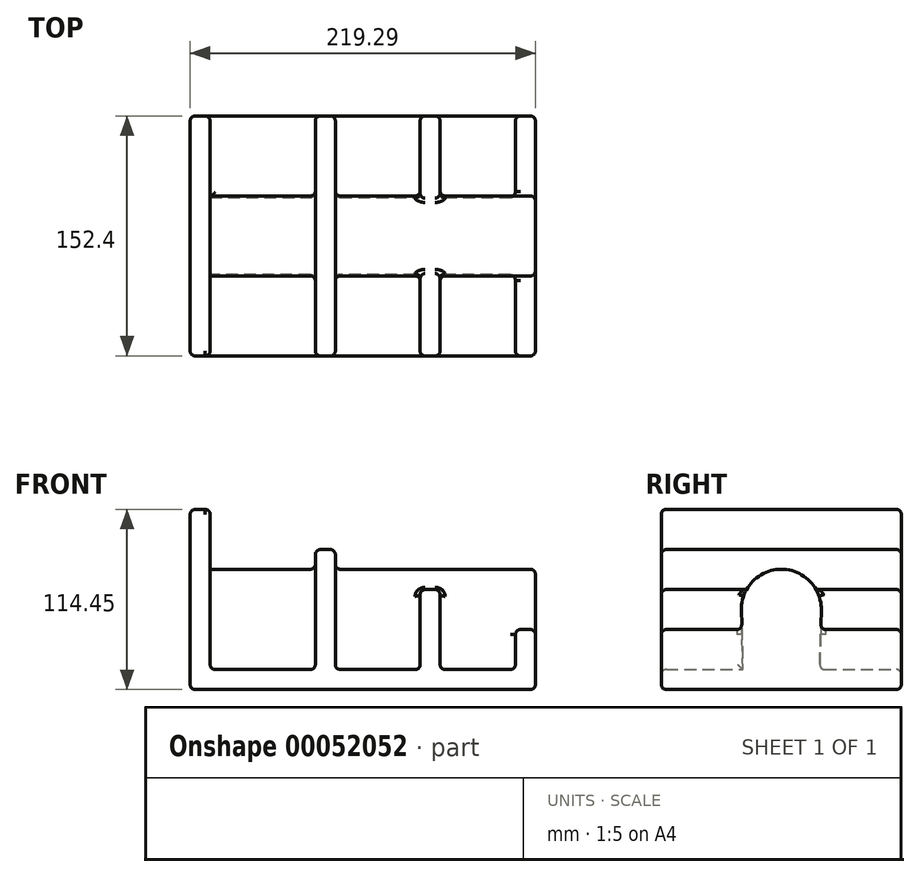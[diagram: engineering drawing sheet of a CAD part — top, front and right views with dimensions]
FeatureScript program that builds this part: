
annotation { "Feature Type Name" : "Feature", "Feature Type Description" : "" }
export const myFeature = defineFeature(function(context is Context, id is Id, definition is map)
    precondition{}
    {
        {
            var Q0;
            Q0=qCreatedBy(makeId("Front.planeOp"),FACE);
            var sketch = newSketch(context, id + "F0", { "sketchPlane" : qUnion([Q0])});
            skLineSegment(sketch, "E0", {"start": v(0, 114.3) * mm, "end": v(0, 0) * mm});
            skLineSegment(sketch, "E1", {"start": v(0, 0) * mm, "end": v(219.3, 0) * mm});
            skLineSegment(sketch, "E2", {"start": v(219.3, 0) * mm, "end": v(219.3, 38.1) * mm});
            skLineSegment(sketch, "E3", {"start": v(219.3, 38.1) * mm, "end": v(206.6, 38.1) * mm});
            skLineSegment(sketch, "E4", {"start": v(206.6, 38.1) * mm, "end": v(206.6, 12.7) * mm});
            skLineSegment(sketch, "E5", {"start": v(206.6, 12.7) * mm, "end": v(158.76, 12.7) * mm});
            skLineSegment(sketch, "E6", {"start": v(158.76, 12.7) * mm, "end": v(158.76, 63.5) * mm});
            skLineSegment(sketch, "E7", {"start": v(158.76, 63.5) * mm, "end": v(146.06, 63.5) * mm});
            skLineSegment(sketch, "E8", {"start": v(146.06, 63.5) * mm, "end": v(146.06, 12.7) * mm});
            skLineSegment(sketch, "E9", {"start": v(146.06, 12.7) * mm, "end": v(92.23, 12.7) * mm});
            skLineSegment(sketch, "E10", {"start": v(92.23, 12.7) * mm, "end": v(92.23, 88.9) * mm});
            skLineSegment(sketch, "E11", {"start": v(92.23, 88.9) * mm, "end": v(79.53, 88.9) * mm});
            skLineSegment(sketch, "E12", {"start": v(79.53, 88.9) * mm, "end": v(79.53, 12.7) * mm});
            skLineSegment(sketch, "E13", {"start": v(79.53, 12.7) * mm, "end": v(12.7, 12.7) * mm});
            skLineSegment(sketch, "E14", {"start": v(12.7, 12.7) * mm, "end": v(12.7, 114.5) * mm});
            skLineSegment(sketch, "E15", {"start": v(12.7, 114.5) * mm, "end": v(0, 114.3) * mm});
            skSolve(sketch);
        }
        {
            var Q0;
            Q0=makeQuery(id+"F0.imprint","IMPRINT",FACE,{"disambiguationData":[TD([[makeQuery(id+"F0.imprint","IMPRINT",EDGE,{"derivedFrom":sQuery(id+"F0.wireOp",EDGE,"E0")}),1.0]])]});
            extrude(context, id + "F1", {"entities" : qUnion([Q0]), "depth" : 152.4 * mm});
        }
        {
            var Q0;
            Q0=makeQuery(id+"F1.opExtrude","SWEPT_FACE",FACE,{"disambiguationData":[OSD([sQuery(id+"F0.wireOp",EDGE,"E14")])]});
            var sketch = newSketch(context, id + "F2", { "sketchPlane" : qUnion([Q0])});
            skArc(sketch, "E16", {"start": v(-50.8, 50.3) * mm, "mid": v(-76.17, 76.4) * mm, "end": v(-101.6, 50.36) * mm});
            skLineSegment(sketch, "E17", {"start": v(-101.6, 50.36) * mm, "end": v(-100.64, 12.7) * mm});
            skLineSegment(sketch, "E18", {"start": v(-100.64, 12.7) * mm, "end": v(-51.85, 12.7) * mm});
            skLineSegment(sketch, "E19", {"start": v(-51.85, 12.7) * mm, "end": v(-50.8, 50.3) * mm});
            skSolve(sketch);
        }
        {
            var Q0;
            Q0 = qSketchRegion(id + "F2", true);
            var Q1;
            Q1=makeQuery(id+"F1.opExtrude","SWEPT_FACE",FACE,{"disambiguationData":[OSD([sQuery(id+"F0.wireOp",EDGE,"E2")])]});
            extrude(context, id + "F3", {"entities" : qUnion([Q0]), "operationType" : NewBodyOperationType.ADD, "endBound" : BoundingType.UP_TO_SURFACE, "endBoundEntityFace" : qUnion([Q1]), "depth" : 25.4 * mm});
        }
        {
            var Q0;
            Q0=makeQuery(id+"F1.opExtrude","CAP_EDGE",EDGE,{"disambiguationData":[OSD([sQuery(id+"F0.wireOp",EDGE,"E11")])],"isStart":false});
            var Q1;
            Q1=makeQuery(id+"F1.opExtrude","CAP_EDGE",EDGE,{"disambiguationData":[OSD([sQuery(id+"F0.wireOp",EDGE,"E7")])],"isStart":false});
            var Q2;
            Q2=makeQuery(id+"F1.opExtrude","CAP_EDGE",EDGE,{"disambiguationData":[OSD([sQuery(id+"F0.wireOp",EDGE,"E3")])],"isStart":true});
            var Q3;
            Q3=makeQuery(id+"F1.opExtrude","CAP_EDGE",EDGE,{"disambiguationData":[OSD([sQuery(id+"F0.wireOp",EDGE,"E14")])],"isStart":false});
            var Q4;
            Q4=makeQuery(id+"F1.opExtrude","CAP_EDGE",EDGE,{"disambiguationData":[OSD([sQuery(id+"F0.wireOp",EDGE,"E10")])],"isStart":true});
            var Q5;
            Q5=makeQuery(id+"F1.opExtrude","CAP_EDGE",EDGE,{"disambiguationData":[OSD([sQuery(id+"F0.wireOp",EDGE,"E6")])],"isStart":false});
            var Q6;
            Q6=makeQuery(id+"F1.opExtrude","CAP_EDGE",EDGE,{"disambiguationData":[OSD([sQuery(id+"F0.wireOp",EDGE,"E9")])],"isStart":true});
            var Q7;
            Q7=makeQuery(id+"F1.opExtrude","CAP_EDGE",EDGE,{"disambiguationData":[OSD([sQuery(id+"F0.wireOp",EDGE,"E1")])],"isStart":true});
            var Q8;
            Q8=makeQuery(id+"F1.opExtrude","CAP_EDGE",EDGE,{"disambiguationData":[OSD([sQuery(id+"F0.wireOp",EDGE,"E8")])],"isStart":true});
            var Q9;
            Q9=makeQuery(id+"F1.opExtrude","SWEPT_EDGE",EDGE,{"disambiguationData":[OSD([sQuery(id+"F0.wireOp",EDGE,"E14"),sQuery(id+"F0.wireOp",EDGE,"E15")])]});
            var Q10;
            Q10=makeQuery(id+"F1.opExtrude","CAP_EDGE",EDGE,{"disambiguationData":[OSD([sQuery(id+"F0.wireOp",EDGE,"E6")])],"isStart":true});
            var Q11;
            Q11=makeQuery(id+"F1.opExtrude","SWEPT_EDGE",EDGE,{"disambiguationData":[OSD([sQuery(id+"F0.wireOp",EDGE,"E0"),sQuery(id+"F0.wireOp",EDGE,"E15")])]});
            var Q12;
            Q12=makeQuery(id+"F1.opExtrude","CAP_EDGE",EDGE,{"disambiguationData":[OSD([sQuery(id+"F0.wireOp",EDGE,"E5")])],"isStart":true});
            var Q13;
            Q13=makeQuery(id+"F1.opExtrude","SWEPT_EDGE",EDGE,{"disambiguationData":[OSD([sQuery(id+"F0.wireOp",EDGE,"E1"),sQuery(id+"F0.wireOp",EDGE,"E2")])]});
            var Q14;
            Q14=makeQuery(id+"F1.opExtrude","CAP_EDGE",EDGE,{"disambiguationData":[OSD([sQuery(id+"F0.wireOp",EDGE,"E13")])],"isStart":true});
            var Q15;
            Q15=makeQuery(id+"F3.opExtrude","CAP_EDGE",EDGE,{"disambiguationData":[OSD([sQuery(id+"F2.wireOp",EDGE,"E16")])],"isStart":false});
            var Q16;
            Q16=makeQuery(id+"F1.opExtrude","CAP_EDGE",EDGE,{"disambiguationData":[OSD([sQuery(id+"F0.wireOp",EDGE,"E12")])],"isStart":true});
            var Q17;
            {var subQ0=sQuery(id+"F0.wireOp",EDGE,"E7");var subQ1=sQuery(id+"F0.wireOp",EDGE,"E6");Q17=makeQuery(id+"F3.boolean.opBoolean","SPLIT",EDGE,{"disambiguationData":[TD([makeQuery(id+"F1.opExtrude","CAP_FACE",FACE,{"disambiguationData":[OSD([sQuery(id+"F0.wireOp",EDGE,"E0"),sQuery(id+"F0.wireOp",EDGE,"E1"),sQuery(id+"F0.wireOp",EDGE,"E2"),sQuery(id+"F0.wireOp",EDGE,"E3"),sQuery(id+"F0.wireOp",EDGE,"E4"),sQuery(id+"F0.wireOp",EDGE,"E5"),subQ1,subQ0,sQuery(id+"F0.wireOp",EDGE,"E8"),sQuery(id+"F0.wireOp",EDGE,"E9"),sQuery(id+"F0.wireOp",EDGE,"E10"),sQuery(id+"F0.wireOp",EDGE,"E11"),sQuery(id+"F0.wireOp",EDGE,"E12"),sQuery(id+"F0.wireOp",EDGE,"E13"),sQuery(id+"F0.wireOp",EDGE,"E14"),sQuery(id+"F0.wireOp",EDGE,"E15")])],"isStart":true})])],"derivedFrom":makeQuery(id+"F1.opExtrude","SWEPT_EDGE",EDGE,{"disambiguationData":[OSD([subQ1,subQ0])]})});}
            var Q18;
            Q18=makeQuery(id+"F1.opExtrude","CAP_EDGE",EDGE,{"disambiguationData":[OSD([sQuery(id+"F0.wireOp",EDGE,"E10")])],"isStart":false});
            var Q19;
            Q19=makeQuery(id+"F1.opExtrude","SWEPT_EDGE",EDGE,{"disambiguationData":[OSD([sQuery(id+"F0.wireOp",EDGE,"E10"),sQuery(id+"F0.wireOp",EDGE,"E11")])]});
            var Q20;
            Q20=makeQuery(id+"F1.opExtrude","SWEPT_EDGE",EDGE,{"disambiguationData":[OSD([sQuery(id+"F0.wireOp",EDGE,"E11"),sQuery(id+"F0.wireOp",EDGE,"E12")])]});
            var Q21;
            Q21=makeQuery(id+"F3.opExtrude","CAP_EDGE",EDGE,{"disambiguationData":[OSD([sQuery(id+"F2.wireOp",EDGE,"E16")])],"isStart":true});
            var Q22;
            {var subQ0=sQuery(id+"F0.wireOp",EDGE,"E8");var subQ1=sQuery(id+"F0.wireOp",EDGE,"E7");Q22=makeQuery(id+"F3.boolean.opBoolean","SPLIT",EDGE,{"disambiguationData":[TD([makeQuery(id+"F1.opExtrude","CAP_FACE",FACE,{"disambiguationData":[OSD([sQuery(id+"F0.wireOp",EDGE,"E0"),sQuery(id+"F0.wireOp",EDGE,"E1"),sQuery(id+"F0.wireOp",EDGE,"E2"),sQuery(id+"F0.wireOp",EDGE,"E3"),sQuery(id+"F0.wireOp",EDGE,"E4"),sQuery(id+"F0.wireOp",EDGE,"E5"),sQuery(id+"F0.wireOp",EDGE,"E6"),subQ1,subQ0,sQuery(id+"F0.wireOp",EDGE,"E9"),sQuery(id+"F0.wireOp",EDGE,"E10"),sQuery(id+"F0.wireOp",EDGE,"E11"),sQuery(id+"F0.wireOp",EDGE,"E12"),sQuery(id+"F0.wireOp",EDGE,"E13"),sQuery(id+"F0.wireOp",EDGE,"E14"),sQuery(id+"F0.wireOp",EDGE,"E15")])],"isStart":false})])],"derivedFrom":makeQuery(id+"F1.opExtrude","SWEPT_EDGE",EDGE,{"disambiguationData":[OSD([subQ1,subQ0])]})});}
            var Q23;
            {var subQ0=sQuery(id+"F2.wireOp",EDGE,"E16");var subQ1=sQuery(id+"F2.wireOp",EDGE,"E19");Q23=makeQuery(id+"F3.boolean.opBoolean","SPLIT",EDGE,{"disambiguationData":[TD([makeQuery(id+"F1.opExtrude","SWEPT_FACE",FACE,{"disambiguationData":[OSD([sQuery(id+"F0.wireOp",EDGE,"E8")])]})])],"derivedFrom":makeQuery(id+"F3.opExtrude","SWEPT_EDGE",EDGE,{"disambiguationData":[OSD([subQ0,subQ1])]})});}
            var Q24;
            {var subQ0=sQuery(id+"F2.wireOp",EDGE,"E19");var subQ1=sQuery(id+"F2.wireOp",EDGE,"E16");Q24=makeQuery(id+"F3.boolean.opBoolean","SPLIT",EDGE,{"disambiguationData":[TD([makeQuery(id+"F1.opExtrude","SWEPT_FACE",FACE,{"disambiguationData":[OSD([sQuery(id+"F0.wireOp",EDGE,"E2")])]})])],"derivedFrom":makeQuery(id+"F3.opExtrude","SWEPT_EDGE",EDGE,{"disambiguationData":[OSD([subQ1,subQ0])]})});}
            var Q25;
            {var subQ0=sQuery(id+"F0.wireOp",EDGE,"E3");var subQ1=sQuery(id+"F0.wireOp",EDGE,"E2");var subQ2=sQuery(id+"F2.wireOp",EDGE,"E19");Q25=makeQuery(id+"F3.boolean.opBoolean","SPLIT",EDGE,{"disambiguationData":[TD([makeQuery(id+"F3.opExtrude","SWEPT_FACE",FACE,{"disambiguationData":[OSD([subQ2])]})])],"derivedFrom":makeQuery(id+"F1.opExtrude","SWEPT_EDGE",EDGE,{"disambiguationData":[OSD([subQ1,subQ0])]})});}
            var Q26;
            {var subQ0=sQuery(id+"F2.wireOp",EDGE,"E17");var subQ1=sQuery(id+"F0.wireOp",EDGE,"E3");var subQ2=sQuery(id+"F0.wireOp",EDGE,"E2");Q26=makeQuery(id+"F3.boolean.opBoolean","SPLIT",EDGE,{"disambiguationData":[TD([makeQuery(id+"F3.opExtrude","SWEPT_FACE",FACE,{"disambiguationData":[OSD([subQ0])]})])],"derivedFrom":makeQuery(id+"F1.opExtrude","SWEPT_EDGE",EDGE,{"disambiguationData":[OSD([subQ2,subQ1])]})});}
            var Q27;
            {var subQ0=sQuery(id+"F0.wireOp",EDGE,"E4");var subQ1=sQuery(id+"F0.wireOp",EDGE,"E3");Q27=makeQuery(id+"F3.boolean.opBoolean","SPLIT",EDGE,{"disambiguationData":[TD([makeQuery(id+"F3.opExtrude","SWEPT_FACE",FACE,{"disambiguationData":[OSD([sQuery(id+"F2.wireOp",EDGE,"E19")])]})])],"derivedFrom":makeQuery(id+"F1.opExtrude","SWEPT_EDGE",EDGE,{"disambiguationData":[OSD([subQ1,subQ0])]})});}
            var Q28;
            {var subQ0=sQuery(id+"F0.wireOp",EDGE,"E4");var subQ1=sQuery(id+"F0.wireOp",EDGE,"E3");Q28=makeQuery(id+"F3.boolean.opBoolean","SPLIT",EDGE,{"disambiguationData":[TD([makeQuery(id+"F3.opExtrude","SWEPT_FACE",FACE,{"disambiguationData":[OSD([sQuery(id+"F2.wireOp",EDGE,"E17")])]})])],"derivedFrom":makeQuery(id+"F1.opExtrude","SWEPT_EDGE",EDGE,{"disambiguationData":[OSD([subQ1,subQ0])]})});}
            var Q29;
            Q29=makeQuery(id+"F3.boolean.opBoolean","INTERSECT",EDGE,{"disambiguationData":[OD(0.0)],"derivedFrom":[makeQuery(id+"F1.opExtrude","SWEPT_FACE",FACE,{"disambiguationData":[OSD([sQuery(id+"F0.wireOp",EDGE,"E7")])]}),makeQuery(id+"F3.opExtrude","SWEPT_FACE",FACE,{"disambiguationData":[OSD([sQuery(id+"F2.wireOp",EDGE,"E16")])]})]});
            var Q30;
            {var subQ0=sQuery(id+"F0.wireOp",EDGE,"E6");var subQ1=sQuery(id+"F0.wireOp",EDGE,"E5");Q30=makeQuery(id+"F3.boolean.opBoolean","SPLIT",EDGE,{"disambiguationData":[TD([makeQuery(id+"F3.opExtrude","SWEPT_FACE",FACE,{"disambiguationData":[OSD([sQuery(id+"F2.wireOp",EDGE,"E19")])]})])],"derivedFrom":makeQuery(id+"F1.opExtrude","SWEPT_EDGE",EDGE,{"disambiguationData":[OSD([subQ1,subQ0])]})});}
            var Q31;
            Q31=makeQuery(id+"F3.boolean.opBoolean","INTERSECT",EDGE,{"derivedFrom":[makeQuery(id+"F1.opExtrude","SWEPT_FACE",FACE,{"disambiguationData":[OSD([sQuery(id+"F0.wireOp",EDGE,"E6")])]}),makeQuery(id+"F3.opExtrude","SWEPT_FACE",FACE,{"disambiguationData":[OSD([sQuery(id+"F2.wireOp",EDGE,"E19")])]})]});
            var Q32;
            Q32=makeQuery(id+"F3.boolean.opBoolean","INTERSECT",EDGE,{"derivedFrom":[makeQuery(id+"F1.opExtrude","SWEPT_FACE",FACE,{"disambiguationData":[OSD([sQuery(id+"F0.wireOp",EDGE,"E3")])]}),makeQuery(id+"F3.opExtrude","SWEPT_FACE",FACE,{"disambiguationData":[OSD([sQuery(id+"F2.wireOp",EDGE,"E19")])]})]});
            var Q33;
            {var subQ0=sQuery(id+"F0.wireOp",EDGE,"E10");var subQ1=sQuery(id+"F0.wireOp",EDGE,"E9");Q33=makeQuery(id+"F3.boolean.opBoolean","SPLIT",EDGE,{"disambiguationData":[TD([makeQuery(id+"F3.opExtrude","SWEPT_FACE",FACE,{"disambiguationData":[OSD([sQuery(id+"F2.wireOp",EDGE,"E19")])]})])],"derivedFrom":makeQuery(id+"F1.opExtrude","SWEPT_EDGE",EDGE,{"disambiguationData":[OSD([subQ1,subQ0])]})});}
            var Q34;
            Q34=makeQuery(id+"F1.opExtrude","CAP_EDGE",EDGE,{"disambiguationData":[OSD([sQuery(id+"F0.wireOp",EDGE,"E5")])],"isStart":false});
            var Q35;
            Q35=makeQuery(id+"F1.opExtrude","CAP_EDGE",EDGE,{"disambiguationData":[OSD([sQuery(id+"F0.wireOp",EDGE,"E13")])],"isStart":false});
            var Q36;
            Q36=makeQuery(id+"F1.opExtrude","CAP_EDGE",EDGE,{"disambiguationData":[OSD([sQuery(id+"F0.wireOp",EDGE,"E4")])],"isStart":false});
            var Q37;
            Q37=makeQuery(id+"F1.opExtrude","CAP_EDGE",EDGE,{"disambiguationData":[OSD([sQuery(id+"F0.wireOp",EDGE,"E12")])],"isStart":false});
            var Q38;
            Q38=makeQuery(id+"F1.opExtrude","CAP_EDGE",EDGE,{"disambiguationData":[OSD([sQuery(id+"F0.wireOp",EDGE,"E3")])],"isStart":false});
            var Q39;
            Q39=makeQuery(id+"F3.boolean.opBoolean","INTERSECT",EDGE,{"disambiguationData":[OD(1.0)],"derivedFrom":[makeQuery(id+"F1.opExtrude","SWEPT_FACE",FACE,{"disambiguationData":[OSD([sQuery(id+"F0.wireOp",EDGE,"E7")])]}),makeQuery(id+"F3.opExtrude","SWEPT_FACE",FACE,{"disambiguationData":[OSD([sQuery(id+"F2.wireOp",EDGE,"E16")])]})]});
            var Q40;
            Q40=makeQuery(id+"F1.opExtrude","CAP_EDGE",EDGE,{"disambiguationData":[OSD([sQuery(id+"F0.wireOp",EDGE,"E15")])],"isStart":false});
            var Q41;
            Q41=makeQuery(id+"F1.opExtrude","CAP_EDGE",EDGE,{"disambiguationData":[OSD([sQuery(id+"F0.wireOp",EDGE,"E11")])],"isStart":true});
            var Q42;
            Q42=makeQuery(id+"F1.opExtrude","CAP_EDGE",EDGE,{"disambiguationData":[OSD([sQuery(id+"F0.wireOp",EDGE,"E2")])],"isStart":true});
            var Q43;
            Q43=makeQuery(id+"F1.opExtrude","CAP_EDGE",EDGE,{"disambiguationData":[OSD([sQuery(id+"F0.wireOp",EDGE,"E0")])],"isStart":true});
            var Q44;
            {var subQ0=sQuery(id+"F0.wireOp",EDGE,"E8");var subQ1=sQuery(id+"F0.wireOp",EDGE,"E7");Q44=makeQuery(id+"F3.boolean.opBoolean","SPLIT",EDGE,{"disambiguationData":[TD([makeQuery(id+"F1.opExtrude","CAP_FACE",FACE,{"disambiguationData":[OSD([sQuery(id+"F0.wireOp",EDGE,"E0"),sQuery(id+"F0.wireOp",EDGE,"E1"),sQuery(id+"F0.wireOp",EDGE,"E2"),sQuery(id+"F0.wireOp",EDGE,"E3"),sQuery(id+"F0.wireOp",EDGE,"E4"),sQuery(id+"F0.wireOp",EDGE,"E5"),sQuery(id+"F0.wireOp",EDGE,"E6"),subQ1,subQ0,sQuery(id+"F0.wireOp",EDGE,"E9"),sQuery(id+"F0.wireOp",EDGE,"E10"),sQuery(id+"F0.wireOp",EDGE,"E11"),sQuery(id+"F0.wireOp",EDGE,"E12"),sQuery(id+"F0.wireOp",EDGE,"E13"),sQuery(id+"F0.wireOp",EDGE,"E14"),sQuery(id+"F0.wireOp",EDGE,"E15")])],"isStart":true})])],"derivedFrom":makeQuery(id+"F1.opExtrude","SWEPT_EDGE",EDGE,{"disambiguationData":[OSD([subQ1,subQ0])]})});}
            var Q45;
            Q45=makeQuery(id+"F1.opExtrude","SWEPT_EDGE",EDGE,{"disambiguationData":[OSD([sQuery(id+"F0.wireOp",EDGE,"E0"),sQuery(id+"F0.wireOp",EDGE,"E1")])]});
            var Q46;
            Q46=makeQuery(id+"F1.opExtrude","CAP_EDGE",EDGE,{"disambiguationData":[OSD([sQuery(id+"F0.wireOp",EDGE,"E14")])],"isStart":true});
            var Q47;
            Q47=makeQuery(id+"F1.opExtrude","CAP_EDGE",EDGE,{"disambiguationData":[OSD([sQuery(id+"F0.wireOp",EDGE,"E4")])],"isStart":true});
            var Q48;
            {var subQ0=sQuery(id+"F0.wireOp",EDGE,"E7");var subQ1=sQuery(id+"F0.wireOp",EDGE,"E6");Q48=makeQuery(id+"F3.boolean.opBoolean","SPLIT",EDGE,{"disambiguationData":[TD([makeQuery(id+"F1.opExtrude","CAP_FACE",FACE,{"disambiguationData":[OSD([sQuery(id+"F0.wireOp",EDGE,"E0"),sQuery(id+"F0.wireOp",EDGE,"E1"),sQuery(id+"F0.wireOp",EDGE,"E2"),sQuery(id+"F0.wireOp",EDGE,"E3"),sQuery(id+"F0.wireOp",EDGE,"E4"),sQuery(id+"F0.wireOp",EDGE,"E5"),subQ1,subQ0,sQuery(id+"F0.wireOp",EDGE,"E8"),sQuery(id+"F0.wireOp",EDGE,"E9"),sQuery(id+"F0.wireOp",EDGE,"E10"),sQuery(id+"F0.wireOp",EDGE,"E11"),sQuery(id+"F0.wireOp",EDGE,"E12"),sQuery(id+"F0.wireOp",EDGE,"E13"),sQuery(id+"F0.wireOp",EDGE,"E14"),sQuery(id+"F0.wireOp",EDGE,"E15")])],"isStart":false})])],"derivedFrom":makeQuery(id+"F1.opExtrude","SWEPT_EDGE",EDGE,{"disambiguationData":[OSD([subQ1,subQ0])]})});}
            var Q49;
            Q49=makeQuery(id+"F1.opExtrude","CAP_EDGE",EDGE,{"disambiguationData":[OSD([sQuery(id+"F0.wireOp",EDGE,"E15")])],"isStart":true});
            var Q50;
            Q50=makeQuery(id+"F1.opExtrude","CAP_EDGE",EDGE,{"disambiguationData":[OSD([sQuery(id+"F0.wireOp",EDGE,"E7")])],"isStart":true});
            var Q51;
            Q51=makeQuery(id+"F1.opExtrude","CAP_EDGE",EDGE,{"disambiguationData":[OSD([sQuery(id+"F0.wireOp",EDGE,"E2")])],"isStart":false});
            var Q52;
            Q52=makeQuery(id+"F1.opExtrude","CAP_EDGE",EDGE,{"disambiguationData":[OSD([sQuery(id+"F0.wireOp",EDGE,"E9")])],"isStart":false});
            var Q53;
            Q53=makeQuery(id+"F1.opExtrude","CAP_EDGE",EDGE,{"disambiguationData":[OSD([sQuery(id+"F0.wireOp",EDGE,"E1")])],"isStart":false});
            var Q54;
            Q54=makeQuery(id+"F1.opExtrude","CAP_EDGE",EDGE,{"disambiguationData":[OSD([sQuery(id+"F0.wireOp",EDGE,"E8")])],"isStart":false});
            var Q55;
            Q55=makeQuery(id+"F1.opExtrude","CAP_EDGE",EDGE,{"disambiguationData":[OSD([sQuery(id+"F0.wireOp",EDGE,"E0")])],"isStart":false});
            var Q56;
            {var subQ0=sQuery(id+"F0.wireOp",EDGE,"E13");var subQ1=sQuery(id+"F0.wireOp",EDGE,"E14");var subQ2=sQuery(id+"F2.wireOp",EDGE,"E19");Q56=makeQuery(id+"F3.boolean.opBoolean","SPLIT",EDGE,{"disambiguationData":[TD([makeQuery(id+"F1.opExtrude","SWEPT_FACE",FACE,{"disambiguationData":[OSD([sQuery(id+"F0.wireOp",EDGE,"E12")])]})])],"derivedFrom":makeQuery(id+"F3.opExtrude","SWEPT_EDGE",EDGE,{"disambiguationData":[OSD([subQ0,subQ1,sQuery(id+"F2.wireOp",EDGE,"E18"),subQ2])]})});}
            var Q57;
            Q57=makeQuery(id+"F3.opExtrude","CAP_EDGE",EDGE,{"disambiguationData":[OSD([sQuery(id+"F2.wireOp",EDGE,"E17")])],"isStart":true});
            var Q58;
            Q58=makeQuery(id+"F3.opExtrude","CAP_EDGE",EDGE,{"disambiguationData":[OSD([sQuery(id+"F2.wireOp",EDGE,"E17")])],"isStart":false});
            var Q59;
            Q59=makeQuery(id+"F3.opExtrude","CAP_EDGE",EDGE,{"disambiguationData":[OSD([sQuery(id+"F2.wireOp",EDGE,"E19")])],"isStart":true});
            var Q60;
            Q60=makeQuery(id+"F3.opExtrude","CAP_EDGE",EDGE,{"disambiguationData":[OSD([sQuery(id+"F2.wireOp",EDGE,"E19")])],"isStart":false});
            var Q61;
            Q61=makeQuery(id+"F3.boolean.opBoolean","INTERSECT",EDGE,{"disambiguationData":[OD(0.0)],"derivedFrom":[makeQuery(id+"F1.opExtrude","SWEPT_FACE",FACE,{"disambiguationData":[OSD([sQuery(id+"F0.wireOp",EDGE,"E6")])]}),makeQuery(id+"F3.opExtrude","SWEPT_FACE",FACE,{"disambiguationData":[OSD([sQuery(id+"F2.wireOp",EDGE,"E16")])]})]});
            var Q62;
            Q62=makeQuery(id+"F3.boolean.opBoolean","INTERSECT",EDGE,{"derivedFrom":[makeQuery(id+"F1.opExtrude","SWEPT_FACE",FACE,{"disambiguationData":[OSD([sQuery(id+"F0.wireOp",EDGE,"E4")])]}),makeQuery(id+"F3.opExtrude","SWEPT_FACE",FACE,{"disambiguationData":[OSD([sQuery(id+"F2.wireOp",EDGE,"E19")])]})]});
            var Q63;
            {var subQ0=sQuery(id+"F0.wireOp",EDGE,"E14");var subQ1=sQuery(id+"F0.wireOp",EDGE,"E13");Q63=makeQuery(id+"F3.boolean.opBoolean","SPLIT",EDGE,{"disambiguationData":[TD([makeQuery(id+"F3.opExtrude","SWEPT_FACE",FACE,{"disambiguationData":[OSD([sQuery(id+"F2.wireOp",EDGE,"E19")])]})])],"derivedFrom":makeQuery(id+"F1.opExtrude","SWEPT_EDGE",EDGE,{"disambiguationData":[OSD([subQ1,subQ0])]})});}
            var Q64;
            {var subQ0=sQuery(id+"F2.wireOp",EDGE,"E17");Q64=makeQuery(id+"F3.boolean.opBoolean","SPLIT",EDGE,{"disambiguationData":[TD([makeQuery(id+"F1.opExtrude","SWEPT_FACE",FACE,{"disambiguationData":[OSD([sQuery(id+"F0.wireOp",EDGE,"E8")])]})])],"derivedFrom":makeQuery(id+"F3.opExtrude","SWEPT_EDGE",EDGE,{"disambiguationData":[OSD([sQuery(id+"F0.wireOp",EDGE,"E13"),sQuery(id+"F0.wireOp",EDGE,"E14"),subQ0,sQuery(id+"F2.wireOp",EDGE,"E18")])]})});}
            var Q65;
            {var subQ0=sQuery(id+"F0.wireOp",EDGE,"E13");var subQ1=sQuery(id+"F0.wireOp",EDGE,"E14");var subQ2=sQuery(id+"F2.wireOp",EDGE,"E17");Q65=makeQuery(id+"F3.boolean.opBoolean","SPLIT",EDGE,{"disambiguationData":[TD([makeQuery(id+"F1.opExtrude","SWEPT_FACE",FACE,{"disambiguationData":[OSD([sQuery(id+"F0.wireOp",EDGE,"E12")])]})])],"derivedFrom":makeQuery(id+"F3.opExtrude","SWEPT_EDGE",EDGE,{"disambiguationData":[OSD([subQ0,subQ1,subQ2,sQuery(id+"F2.wireOp",EDGE,"E18")])]})});}
            var Q66;
            Q66=makeQuery(id+"F3.boolean.opBoolean","INTERSECT",EDGE,{"derivedFrom":[makeQuery(id+"F1.opExtrude","SWEPT_FACE",FACE,{"disambiguationData":[OSD([sQuery(id+"F0.wireOp",EDGE,"E12")])]}),makeQuery(id+"F3.opExtrude","SWEPT_FACE",FACE,{"disambiguationData":[OSD([sQuery(id+"F2.wireOp",EDGE,"E19")])]})]});
            var Q67;
            {var subQ0=sQuery(id+"F0.wireOp",EDGE,"E5");var subQ1=sQuery(id+"F0.wireOp",EDGE,"E4");Q67=makeQuery(id+"F3.boolean.opBoolean","SPLIT",EDGE,{"disambiguationData":[TD([makeQuery(id+"F3.opExtrude","SWEPT_FACE",FACE,{"disambiguationData":[OSD([sQuery(id+"F2.wireOp",EDGE,"E19")])]})])],"derivedFrom":makeQuery(id+"F1.opExtrude","SWEPT_EDGE",EDGE,{"disambiguationData":[OSD([subQ1,subQ0])]})});}
            var Q68;
            {var subQ0=sQuery(id+"F0.wireOp",EDGE,"E5");var subQ1=sQuery(id+"F0.wireOp",EDGE,"E4");Q68=makeQuery(id+"F3.boolean.opBoolean","SPLIT",EDGE,{"disambiguationData":[TD([makeQuery(id+"F3.opExtrude","SWEPT_FACE",FACE,{"disambiguationData":[OSD([sQuery(id+"F2.wireOp",EDGE,"E17")])]})])],"derivedFrom":makeQuery(id+"F1.opExtrude","SWEPT_EDGE",EDGE,{"disambiguationData":[OSD([subQ1,subQ0])]})});}
            var Q69;
            Q69=makeQuery(id+"F3.boolean.opBoolean","INTERSECT",EDGE,{"derivedFrom":[makeQuery(id+"F1.opExtrude","SWEPT_FACE",FACE,{"disambiguationData":[OSD([sQuery(id+"F0.wireOp",EDGE,"E8")])]}),makeQuery(id+"F3.opExtrude","SWEPT_FACE",FACE,{"disambiguationData":[OSD([sQuery(id+"F2.wireOp",EDGE,"E17")])]})]});
            var Q70;
            Q70=makeQuery(id+"F3.boolean.opBoolean","INTERSECT",EDGE,{"disambiguationData":[OD(1.0)],"derivedFrom":[makeQuery(id+"F1.opExtrude","SWEPT_FACE",FACE,{"disambiguationData":[OSD([sQuery(id+"F0.wireOp",EDGE,"E6")])]}),makeQuery(id+"F3.opExtrude","SWEPT_FACE",FACE,{"disambiguationData":[OSD([sQuery(id+"F2.wireOp",EDGE,"E16")])]})]});
            var Q71;
            Q71=makeQuery(id+"F3.boolean.opBoolean","INTERSECT",EDGE,{"derivedFrom":[makeQuery(id+"F1.opExtrude","SWEPT_FACE",FACE,{"disambiguationData":[OSD([sQuery(id+"F0.wireOp",EDGE,"E12")])]}),makeQuery(id+"F3.opExtrude","SWEPT_FACE",FACE,{"disambiguationData":[OSD([sQuery(id+"F2.wireOp",EDGE,"E16")])]})]});
            var Q72;
            {var subQ0=sQuery(id+"F2.wireOp",EDGE,"E16");var subQ1=sQuery(id+"F2.wireOp",EDGE,"E17");Q72=makeQuery(id+"F3.boolean.opBoolean","SPLIT",EDGE,{"disambiguationData":[TD([makeQuery(id+"F1.opExtrude","SWEPT_FACE",FACE,{"disambiguationData":[OSD([sQuery(id+"F0.wireOp",EDGE,"E12")])]})])],"derivedFrom":makeQuery(id+"F3.opExtrude","SWEPT_EDGE",EDGE,{"disambiguationData":[OSD([subQ0,subQ1])]})});}
            var Q73;
            {var subQ0=sQuery(id+"F0.wireOp",EDGE,"E10");var subQ1=sQuery(id+"F0.wireOp",EDGE,"E9");Q73=makeQuery(id+"F3.boolean.opBoolean","SPLIT",EDGE,{"disambiguationData":[TD([makeQuery(id+"F3.opExtrude","SWEPT_FACE",FACE,{"disambiguationData":[OSD([sQuery(id+"F2.wireOp",EDGE,"E17")])]})])],"derivedFrom":makeQuery(id+"F1.opExtrude","SWEPT_EDGE",EDGE,{"disambiguationData":[OSD([subQ1,subQ0])]})});}
            var Q74;
            {var subQ0=sQuery(id+"F0.wireOp",EDGE,"E6");var subQ1=sQuery(id+"F0.wireOp",EDGE,"E5");Q74=makeQuery(id+"F3.boolean.opBoolean","SPLIT",EDGE,{"disambiguationData":[TD([makeQuery(id+"F3.opExtrude","SWEPT_FACE",FACE,{"disambiguationData":[OSD([sQuery(id+"F2.wireOp",EDGE,"E17")])]})])],"derivedFrom":makeQuery(id+"F1.opExtrude","SWEPT_EDGE",EDGE,{"disambiguationData":[OSD([subQ1,subQ0])]})});}
            var Q75;
            Q75=makeQuery(id+"F3.boolean.opBoolean","INTERSECT",EDGE,{"derivedFrom":[makeQuery(id+"F1.opExtrude","SWEPT_FACE",FACE,{"disambiguationData":[OSD([sQuery(id+"F0.wireOp",EDGE,"E8")])]}),makeQuery(id+"F3.opExtrude","SWEPT_FACE",FACE,{"disambiguationData":[OSD([sQuery(id+"F2.wireOp",EDGE,"E19")])]})]});
            var Q76;
            Q76=makeQuery(id+"F3.boolean.opBoolean","INTERSECT",EDGE,{"derivedFrom":[makeQuery(id+"F1.opExtrude","SWEPT_FACE",FACE,{"disambiguationData":[OSD([sQuery(id+"F0.wireOp",EDGE,"E10")])]}),makeQuery(id+"F3.opExtrude","SWEPT_FACE",FACE,{"disambiguationData":[OSD([sQuery(id+"F2.wireOp",EDGE,"E17")])]})]});
            var Q77;
            {var subQ0=sQuery(id+"F2.wireOp",EDGE,"E19");Q77=makeQuery(id+"F3.boolean.opBoolean","SPLIT",EDGE,{"disambiguationData":[TD([makeQuery(id+"F1.opExtrude","SWEPT_FACE",FACE,{"disambiguationData":[OSD([sQuery(id+"F0.wireOp",EDGE,"E4")])]})])],"derivedFrom":makeQuery(id+"F3.opExtrude","SWEPT_EDGE",EDGE,{"disambiguationData":[OSD([sQuery(id+"F0.wireOp",EDGE,"E13"),sQuery(id+"F0.wireOp",EDGE,"E14"),sQuery(id+"F2.wireOp",EDGE,"E18"),subQ0])]})});}
            var Q78;
            Q78=makeQuery(id+"F3.boolean.opBoolean","INTERSECT",EDGE,{"derivedFrom":[makeQuery(id+"F1.opExtrude","SWEPT_FACE",FACE,{"disambiguationData":[OSD([sQuery(id+"F0.wireOp",EDGE,"E3")])]}),makeQuery(id+"F3.opExtrude","SWEPT_FACE",FACE,{"disambiguationData":[OSD([sQuery(id+"F2.wireOp",EDGE,"E17")])]})]});
            var Q79;
            {var subQ0=sQuery(id+"F2.wireOp",EDGE,"E17");var subQ1=sQuery(id+"F2.wireOp",EDGE,"E16");Q79=makeQuery(id+"F3.boolean.opBoolean","SPLIT",EDGE,{"disambiguationData":[TD([makeQuery(id+"F1.opExtrude","SWEPT_FACE",FACE,{"disambiguationData":[OSD([sQuery(id+"F0.wireOp",EDGE,"E2")])]})])],"derivedFrom":makeQuery(id+"F3.opExtrude","SWEPT_EDGE",EDGE,{"disambiguationData":[OSD([subQ1,subQ0])]})});}
            var Q80;
            {var subQ0=sQuery(id+"F2.wireOp",EDGE,"E16");var subQ1=sQuery(id+"F2.wireOp",EDGE,"E19");Q80=makeQuery(id+"F3.boolean.opBoolean","SPLIT",EDGE,{"disambiguationData":[TD([makeQuery(id+"F1.opExtrude","SWEPT_FACE",FACE,{"disambiguationData":[OSD([sQuery(id+"F0.wireOp",EDGE,"E12")])]})])],"derivedFrom":makeQuery(id+"F3.opExtrude","SWEPT_EDGE",EDGE,{"disambiguationData":[OSD([subQ0,subQ1])]})});}
            var Q81;
            Q81=makeQuery(id+"F3.boolean.opBoolean","INTERSECT",EDGE,{"derivedFrom":[makeQuery(id+"F1.opExtrude","SWEPT_FACE",FACE,{"disambiguationData":[OSD([sQuery(id+"F0.wireOp",EDGE,"E4")])]}),makeQuery(id+"F3.opExtrude","SWEPT_FACE",FACE,{"disambiguationData":[OSD([sQuery(id+"F2.wireOp",EDGE,"E17")])]})]});
            var Q82;
            {var subQ0=sQuery(id+"F2.wireOp",EDGE,"E19");Q82=makeQuery(id+"F3.boolean.opBoolean","SPLIT",EDGE,{"disambiguationData":[TD([makeQuery(id+"F1.opExtrude","SWEPT_FACE",FACE,{"disambiguationData":[OSD([sQuery(id+"F0.wireOp",EDGE,"E8")])]})])],"derivedFrom":makeQuery(id+"F3.opExtrude","SWEPT_EDGE",EDGE,{"disambiguationData":[OSD([sQuery(id+"F0.wireOp",EDGE,"E13"),sQuery(id+"F0.wireOp",EDGE,"E14"),sQuery(id+"F2.wireOp",EDGE,"E18"),subQ0])]})});}
            var Q83;
            Q83=makeQuery(id+"F3.boolean.opBoolean","INTERSECT",EDGE,{"derivedFrom":[makeQuery(id+"F1.opExtrude","SWEPT_FACE",FACE,{"disambiguationData":[OSD([sQuery(id+"F0.wireOp",EDGE,"E6")])]}),makeQuery(id+"F3.opExtrude","SWEPT_FACE",FACE,{"disambiguationData":[OSD([sQuery(id+"F2.wireOp",EDGE,"E17")])]})]});
            var Q84;
            {var subQ0=sQuery(id+"F2.wireOp",EDGE,"E17");Q84=makeQuery(id+"F3.boolean.opBoolean","SPLIT",EDGE,{"disambiguationData":[TD([makeQuery(id+"F1.opExtrude","SWEPT_FACE",FACE,{"disambiguationData":[OSD([sQuery(id+"F0.wireOp",EDGE,"E4")])]})])],"derivedFrom":makeQuery(id+"F3.opExtrude","SWEPT_EDGE",EDGE,{"disambiguationData":[OSD([sQuery(id+"F0.wireOp",EDGE,"E13"),sQuery(id+"F0.wireOp",EDGE,"E14"),subQ0,sQuery(id+"F2.wireOp",EDGE,"E18")])]})});}
            var Q85;
            Q85=makeQuery(id+"F3.boolean.opBoolean","INTERSECT",EDGE,{"derivedFrom":[makeQuery(id+"F1.opExtrude","SWEPT_FACE",FACE,{"disambiguationData":[OSD([sQuery(id+"F0.wireOp",EDGE,"E12")])]}),makeQuery(id+"F3.opExtrude","SWEPT_FACE",FACE,{"disambiguationData":[OSD([sQuery(id+"F2.wireOp",EDGE,"E17")])]})]});
            var Q86;
            {var subQ0=sQuery(id+"F2.wireOp",EDGE,"E16");var subQ1=sQuery(id+"F2.wireOp",EDGE,"E17");Q86=makeQuery(id+"F3.boolean.opBoolean","SPLIT",EDGE,{"disambiguationData":[TD([makeQuery(id+"F1.opExtrude","SWEPT_FACE",FACE,{"disambiguationData":[OSD([sQuery(id+"F0.wireOp",EDGE,"E8")])]})])],"derivedFrom":makeQuery(id+"F3.opExtrude","SWEPT_EDGE",EDGE,{"disambiguationData":[OSD([subQ0,subQ1])]})});}
            var Q87;
            {var subQ0=sQuery(id+"F0.wireOp",EDGE,"E13");var subQ1=sQuery(id+"F0.wireOp",EDGE,"E12");Q87=makeQuery(id+"F3.boolean.opBoolean","SPLIT",EDGE,{"disambiguationData":[TD([makeQuery(id+"F3.opExtrude","SWEPT_FACE",FACE,{"disambiguationData":[OSD([sQuery(id+"F2.wireOp",EDGE,"E19")])]})])],"derivedFrom":makeQuery(id+"F1.opExtrude","SWEPT_EDGE",EDGE,{"disambiguationData":[OSD([subQ1,subQ0])]})});}
            var Q88;
            Q88=makeQuery(id+"F3.boolean.opBoolean","INTERSECT",EDGE,{"disambiguationData":[OD(1.0)],"derivedFrom":[makeQuery(id+"F1.opExtrude","SWEPT_FACE",FACE,{"disambiguationData":[OSD([sQuery(id+"F0.wireOp",EDGE,"E8")])]}),makeQuery(id+"F3.opExtrude","SWEPT_FACE",FACE,{"disambiguationData":[OSD([sQuery(id+"F2.wireOp",EDGE,"E16")])]})]});
            var Q89;
            Q89=makeQuery(id+"F3.boolean.opBoolean","INTERSECT",EDGE,{"derivedFrom":[makeQuery(id+"F1.opExtrude","SWEPT_FACE",FACE,{"disambiguationData":[OSD([sQuery(id+"F0.wireOp",EDGE,"E10")])]}),makeQuery(id+"F3.opExtrude","SWEPT_FACE",FACE,{"disambiguationData":[OSD([sQuery(id+"F2.wireOp",EDGE,"E19")])]})]});
            var Q90;
            Q90=makeQuery(id+"F3.boolean.opBoolean","INTERSECT",EDGE,{"disambiguationData":[OD(0.0)],"derivedFrom":[makeQuery(id+"F1.opExtrude","SWEPT_FACE",FACE,{"disambiguationData":[OSD([sQuery(id+"F0.wireOp",EDGE,"E8")])]}),makeQuery(id+"F3.opExtrude","SWEPT_FACE",FACE,{"disambiguationData":[OSD([sQuery(id+"F2.wireOp",EDGE,"E16")])]})]});
            var Q91;
            Q91=makeQuery(id+"F3.boolean.opBoolean","INTERSECT",EDGE,{"derivedFrom":[makeQuery(id+"F1.opExtrude","SWEPT_FACE",FACE,{"disambiguationData":[OSD([sQuery(id+"F0.wireOp",EDGE,"E10")])]}),makeQuery(id+"F3.opExtrude","SWEPT_FACE",FACE,{"disambiguationData":[OSD([sQuery(id+"F2.wireOp",EDGE,"E16")])]})]});
            var Q92;
            {var subQ0=sQuery(id+"F0.wireOp",EDGE,"E9");var subQ1=sQuery(id+"F0.wireOp",EDGE,"E8");Q92=makeQuery(id+"F3.boolean.opBoolean","SPLIT",EDGE,{"disambiguationData":[TD([makeQuery(id+"F3.opExtrude","SWEPT_FACE",FACE,{"disambiguationData":[OSD([sQuery(id+"F2.wireOp",EDGE,"E19")])]})])],"derivedFrom":makeQuery(id+"F1.opExtrude","SWEPT_EDGE",EDGE,{"disambiguationData":[OSD([subQ1,subQ0])]})});}
            var Q93;
            {var subQ0=sQuery(id+"F0.wireOp",EDGE,"E13");var subQ1=sQuery(id+"F0.wireOp",EDGE,"E12");Q93=makeQuery(id+"F3.boolean.opBoolean","SPLIT",EDGE,{"disambiguationData":[TD([makeQuery(id+"F3.opExtrude","SWEPT_FACE",FACE,{"disambiguationData":[OSD([sQuery(id+"F2.wireOp",EDGE,"E17")])]})])],"derivedFrom":makeQuery(id+"F1.opExtrude","SWEPT_EDGE",EDGE,{"disambiguationData":[OSD([subQ1,subQ0])]})});}
            var Q94;
            {var subQ0=sQuery(id+"F0.wireOp",EDGE,"E9");var subQ1=sQuery(id+"F0.wireOp",EDGE,"E8");Q94=makeQuery(id+"F3.boolean.opBoolean","SPLIT",EDGE,{"disambiguationData":[TD([makeQuery(id+"F3.opExtrude","SWEPT_FACE",FACE,{"disambiguationData":[OSD([sQuery(id+"F2.wireOp",EDGE,"E17")])]})])],"derivedFrom":makeQuery(id+"F1.opExtrude","SWEPT_EDGE",EDGE,{"disambiguationData":[OSD([subQ1,subQ0])]})});}
            var Q95;
            {var subQ0=sQuery(id+"F0.wireOp",EDGE,"E14");var subQ1=sQuery(id+"F0.wireOp",EDGE,"E13");Q95=makeQuery(id+"F3.boolean.opBoolean","SPLIT",EDGE,{"disambiguationData":[TD([makeQuery(id+"F3.opExtrude","SWEPT_FACE",FACE,{"disambiguationData":[OSD([sQuery(id+"F2.wireOp",EDGE,"E17")])]})])],"derivedFrom":makeQuery(id+"F1.opExtrude","SWEPT_EDGE",EDGE,{"disambiguationData":[OSD([subQ1,subQ0])]})});}
            fillet(context, id + "F4", {"entities" : qUnion([Q0, Q1, Q2, Q3, Q4, Q5, Q6, Q7, Q8, Q9, Q10, Q11, Q12, Q13, Q14, Q15, Q16, Q17, Q18, Q19, Q20, Q21, Q22, Q23, Q24, Q25, Q26, Q27, Q28, Q29, Q30, Q31, Q32, Q33, Q34, Q35, Q36, Q37, Q38, Q39, Q40, Q41, Q42, Q43, Q44, Q45, Q46, Q47, Q48, Q49, Q50, Q51, Q52, Q53, Q54, Q55, Q56, Q57, Q58, Q59, Q60, Q61, Q62, Q63, Q64, Q65, Q66, Q67, Q68, Q69, Q70, Q71, Q72, Q73, Q74, Q75, Q76, Q77, Q78, Q79, Q80, Q81, Q82, Q83, Q84, Q85, Q86, Q87, Q88, Q89, Q90, Q91, Q92, Q93, Q94, Q95]), "radius" : 3.17 * mm, "tangentPropagation" : true, "allowEdgeOverflow" : false});
        }
    });
